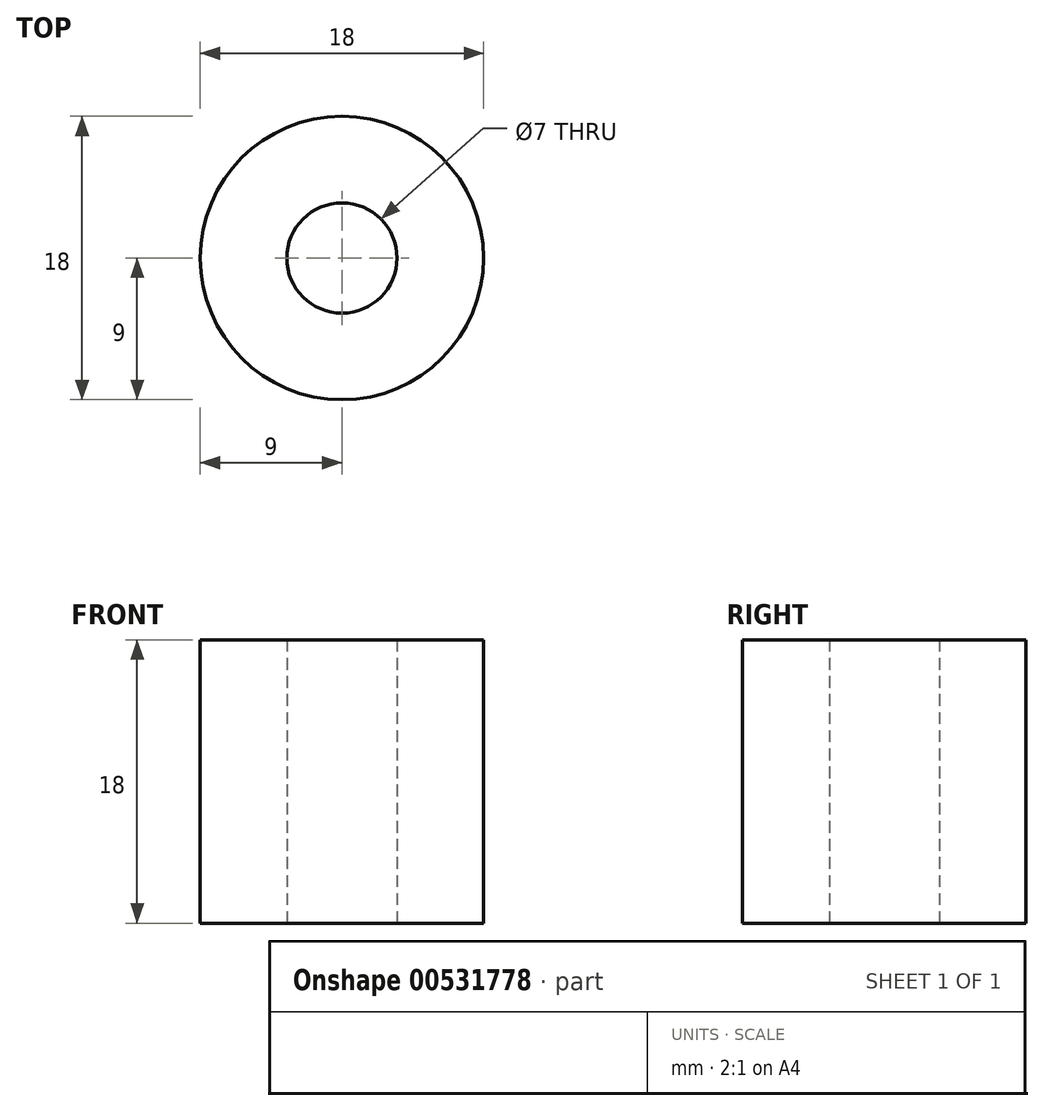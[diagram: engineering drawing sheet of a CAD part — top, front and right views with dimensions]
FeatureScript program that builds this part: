
annotation { "Feature Type Name" : "Feature", "Feature Type Description" : "" }
export const myFeature = defineFeature(function(context is Context, id is Id, definition is map)
    precondition{}
    {
        {
            var Q0;
            Q0=qCreatedBy(makeId("Top.planeOp"),FACE);
            var sketch = newSketch(context, id + "F0", { "sketchPlane" : qUnion([Q0])});
            skCircle(sketch, "E0", {"center": v(0, 0) * mm, "radius": 9 * mm});
            skCircle(sketch, "E1", {"center": v(0, 0) * mm, "radius": 3.5 * mm});
            skSolve(sketch);
        }
        {
            var Q0;
            Q0=makeQuery(id+"F0.imprint","IMPRINT",FACE,{"disambiguationData":[TD([[makeQuery(id+"F0.imprint","IMPRINT",EDGE,{"derivedFrom":sQuery(id+"F0.wireOp",EDGE,"E0")}),1.0]])]});
            extrude(context, id + "F1", {"entities" : qUnion([Q0]), "depth" : 18 * mm, "offsetDistance" : 25 * mm});
        }
    });
